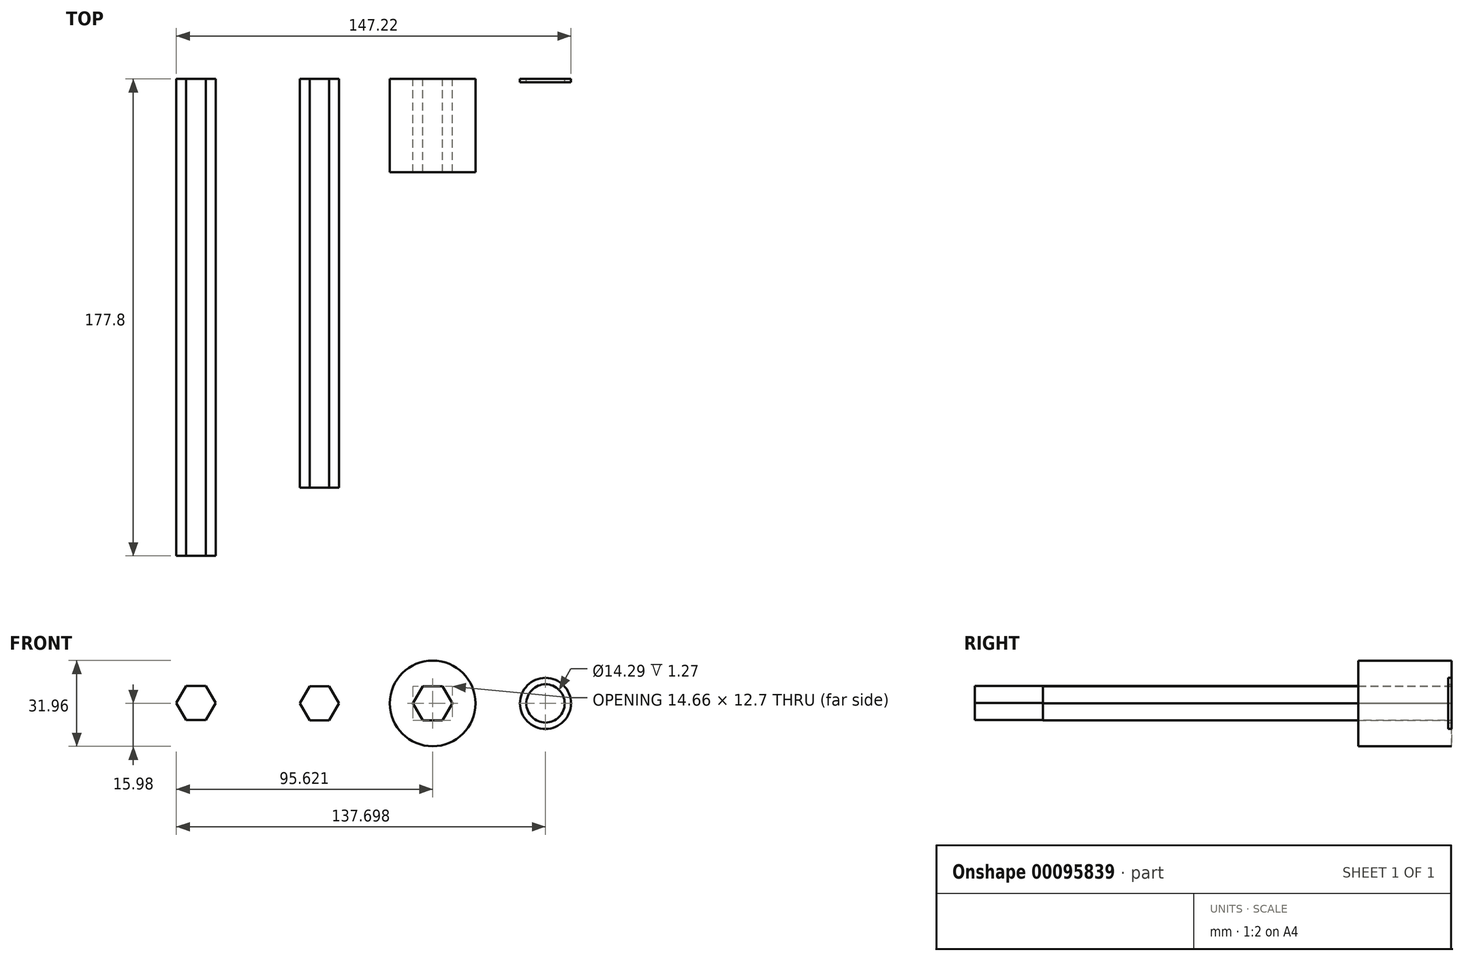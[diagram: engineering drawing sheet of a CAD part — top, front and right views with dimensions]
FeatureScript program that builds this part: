
annotation { "Feature Type Name" : "Feature", "Feature Type Description" : "" }
export const myFeature = defineFeature(function(context is Context, id is Id, definition is map)
    precondition{}
    {
        {
            var Q0;
            Q0=qCreatedBy(makeId("Front.planeOp"),FACE);
            var sketch = newSketch(context, id + "F0", { "sketchPlane" : qUnion([Q0])});
            skCircle(sketch, "E0.cCircle", {"center": v(0, 0) * mm, "radius": 6.35 * mm, "construction": true});
            skLineSegment(sketch, "E0.0", {"start": v(3.65, 6.36) * mm, "end": v(7.33, 0.02) * mm});
            skLineSegment(sketch, "E0.1", {"start": v(7.33, 0.02) * mm, "end": v(3.68, -6.34) * mm});
            skLineSegment(sketch, "E0.2", {"start": v(3.68, -6.34) * mm, "end": v(-3.65, -6.36) * mm});
            skLineSegment(sketch, "E0.3", {"start": v(-3.65, -6.36) * mm, "end": v(-7.33, -0.02) * mm});
            skLineSegment(sketch, "E0.4", {"start": v(-7.33, -0.02) * mm, "end": v(-3.68, 6.34) * mm});
            skLineSegment(sketch, "E0.5", {"start": v(-3.68, 6.34) * mm, "end": v(3.65, 6.36) * mm});
            skPoint(sketch, "E0.0.midPoint", {"position": v(5.5, 3.19) * mm});
            skCircle(sketch, "E1.cCircle", {"center": v(-46.05, 0.17) * mm, "radius": 6.35 * mm, "construction": true});
            skLineSegment(sketch, "E1.0", {"start": v(-42.4, 6.52) * mm, "end": v(-38.72, 0.18) * mm});
            skLineSegment(sketch, "E1.1", {"start": v(-38.72, 0.18) * mm, "end": v(-42.37, -6.18) * mm});
            skLineSegment(sketch, "E1.2", {"start": v(-42.37, -6.18) * mm, "end": v(-49.7, -6.2) * mm});
            skLineSegment(sketch, "E1.3", {"start": v(-49.7, -6.2) * mm, "end": v(-53.38, 0.15) * mm});
            skLineSegment(sketch, "E1.4", {"start": v(-53.38, 0.15) * mm, "end": v(-49.73, 6.5) * mm});
            skLineSegment(sketch, "E1.5", {"start": v(-49.73, 6.5) * mm, "end": v(-42.4, 6.52) * mm});
            skPoint(sketch, "E1.0.midPoint", {"position": v(-40.56, 3.35) * mm});
            skSolve(sketch);
        }
        {
            var Q0;
            Q0=makeQuery(id+"F0.imprint","IMPRINT",FACE,{"disambiguationData":[TD([[makeQuery(id+"F0.imprint","IMPRINT",EDGE,{"derivedFrom":sQuery(id+"F0.wireOp",EDGE,"E0.0")}),-1.0]])]});
            extrude(context, id + "F1", {"entities" : qUnion([Q0]), "depth" : 152.4 * mm});
        }
        {
            var Q0;
            Q0=makeQuery(id+"F0.imprint","IMPRINT",FACE,{"disambiguationData":[TD([[makeQuery(id+"F0.imprint","IMPRINT",EDGE,{"derivedFrom":sQuery(id+"F0.wireOp",EDGE,"E1.0")}),-1.0]])]});
            extrude(context, id + "F2", {"entities" : qUnion([Q0]), "depth" : 177.8 * mm});
        }
        {
            var Q0;
            Q0=qCreatedBy(makeId("Front.planeOp"),FACE);
            var sketch = newSketch(context, id + "F3", { "sketchPlane" : qUnion([Q0])});
            skCircle(sketch, "E2.cCircle", {"center": v(42.24, 0) * mm, "radius": 6.35 * mm, "construction": true});
            skLineSegment(sketch, "E2.0", {"start": v(38.58, 6.35) * mm, "end": v(45.9, 6.35) * mm});
            skLineSegment(sketch, "E2.1", {"start": v(45.9, 6.35) * mm, "end": v(49.57, 0) * mm});
            skLineSegment(sketch, "E2.2", {"start": v(49.57, 0) * mm, "end": v(45.9, -6.35) * mm});
            skLineSegment(sketch, "E2.3", {"start": v(45.9, -6.35) * mm, "end": v(38.58, -6.35) * mm});
            skLineSegment(sketch, "E2.4", {"start": v(38.58, -6.35) * mm, "end": v(34.9, 0) * mm});
            skLineSegment(sketch, "E2.5", {"start": v(34.9, 0) * mm, "end": v(38.58, 6.35) * mm});
            skPoint(sketch, "E2.0.midPoint", {"position": v(42.24, 6.35) * mm});
            skCircle(sketch, "E3", {"center": v(42.24, 0) * mm, "radius": 15.98 * mm});
            skSolve(sketch);
        }
        {
            var Q0;
            Q0=qSketchRegion(id+"F3",true);
            extrude(context, id + "F4", {"entities" : qUnion([Q0]), "depth" : 34.8 * mm});
        }
        {
            var Q0;
            Q0=qCreatedBy(makeId("Front.planeOp"),FACE);
            var sketch = newSketch(context, id + "F5", { "sketchPlane" : qUnion([Q0])});
            skCircle(sketch, "E4", {"center": v(84.32, 0) * mm, "radius": 7.14 * mm});
            skCircle(sketch, "E5", {"center": v(84.32, 0) * mm, "radius": 9.53 * mm});
            skSolve(sketch);
        }
        {
            var Q0;
            Q0=qSketchRegion(id+"F5",true);
            extrude(context, id + "F6", {"entities" : qUnion([Q0]), "depth" : 1.27 * mm});
        }
    });
